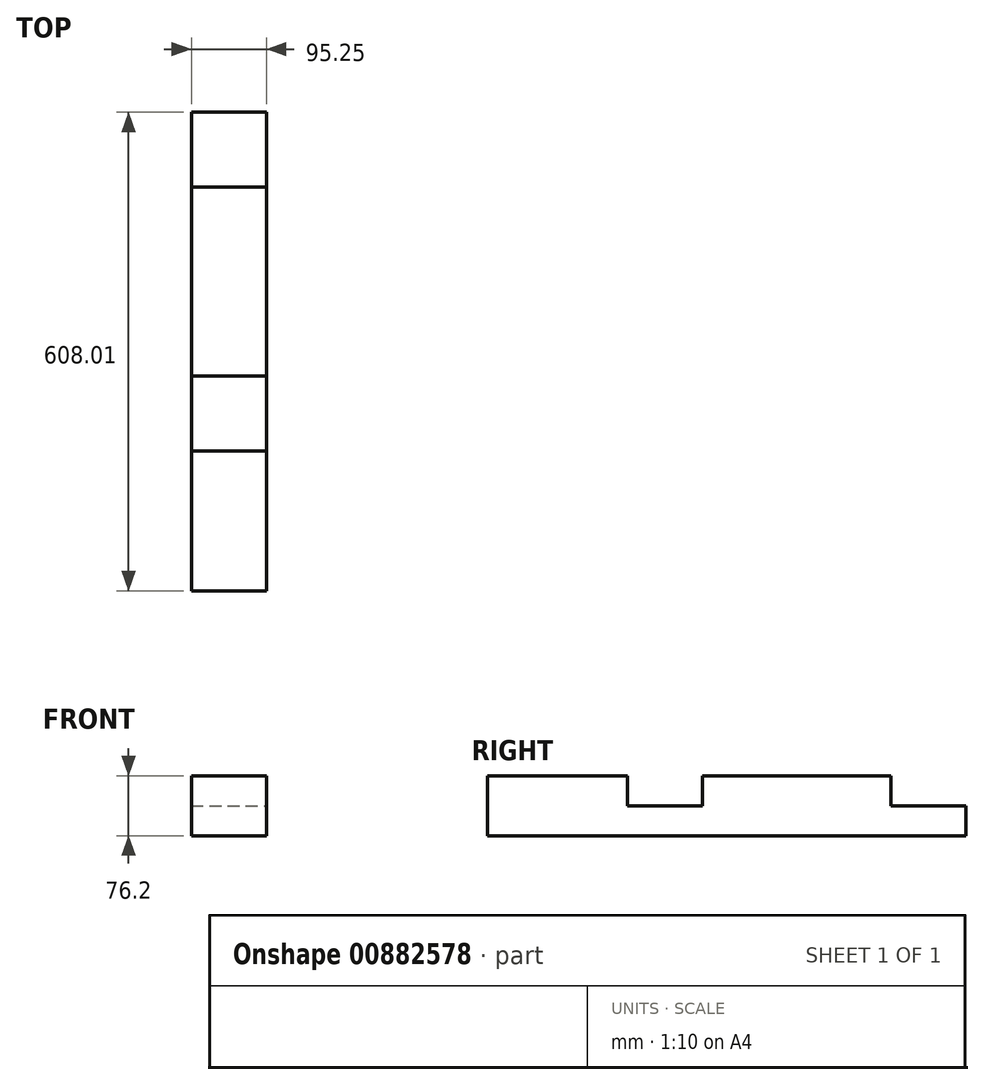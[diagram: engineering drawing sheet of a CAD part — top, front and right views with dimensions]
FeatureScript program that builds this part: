
annotation { "Feature Type Name" : "Feature", "Feature Type Description" : "" }
export const myFeature = defineFeature(function(context is Context, id is Id, definition is map)
    precondition{}
    {
        {
            var Q0;
            Q0=qCreatedBy(makeId("Front.planeOp"),FACE);
            var sketch = newSketch(context, id + "F0", { "sketchPlane" : qUnion([Q0])});
            skLineSegment(sketch, "E0.bottom", {"start": v(0, 0) * mm, "end": v(95.25, 0) * mm});
            skLineSegment(sketch, "E0.top", {"start": v(0, -76.2) * mm, "end": v(95.25, -76.2) * mm});
            skLineSegment(sketch, "E0.left", {"start": v(0, 0) * mm, "end": v(0, -76.2) * mm});
            skLineSegment(sketch, "E0.right", {"start": v(95.25, 0) * mm, "end": v(95.25, -76.2) * mm});
            skSolve(sketch);
        }
        {
            var Q0;
            Q0=qSketchRegion(id+"F0",true);
            extrude(context, id + "F1", {"entities" : qUnion([Q0]), "depth" : 608 * mm, "offsetDistance" : 25.4 * mm});
        }
        {
            var Q0;
            Q0=makeQuery(id+"F1.opExtrude","SWEPT_FACE",FACE,{"disambiguationData":[OSD([sQuery(id+"F0.wireOp",EDGE,"E0.bottom")])]});
            var sketch = newSketch(context, id + "F2", { "sketchPlane" : qUnion([Q0])});
            skLineSegment(sketch, "E1.bottom", {"start": v(0, 0) * mm, "end": v(95.25, 0) * mm});
            skLineSegment(sketch, "E1.top", {"start": v(0, -95.25) * mm, "end": v(95.25, -95.25) * mm});
            skLineSegment(sketch, "E1.left", {"start": v(0, 0) * mm, "end": v(0, -95.25) * mm});
            skLineSegment(sketch, "E1.right", {"start": v(95.25, 0) * mm, "end": v(95.25, -95.25) * mm});
            skLineSegment(sketch, "E2.bottom", {"start": v(0, -334.96) * mm, "end": v(95.25, -334.96) * mm});
            skLineSegment(sketch, "E2.top", {"start": v(0, -430.21) * mm, "end": v(95.25, -430.21) * mm});
            skLineSegment(sketch, "E2.left", {"start": v(0, -334.96) * mm, "end": v(0, -430.21) * mm});
            skLineSegment(sketch, "E2.right", {"start": v(95.25, -334.96) * mm, "end": v(95.25, -430.21) * mm});
            skSolve(sketch);
        }
        {
            var Q0;
            Q0 = qSketchRegion(id + "F2", true);
            extrude(context, id + "F3", {"entities" : qUnion([Q0]), "operationType" : NewBodyOperationType.REMOVE, "oppositeDirection" : true, "depth" : 38.1 * mm, "offsetDistance" : 25.4 * mm});
        }
    });
